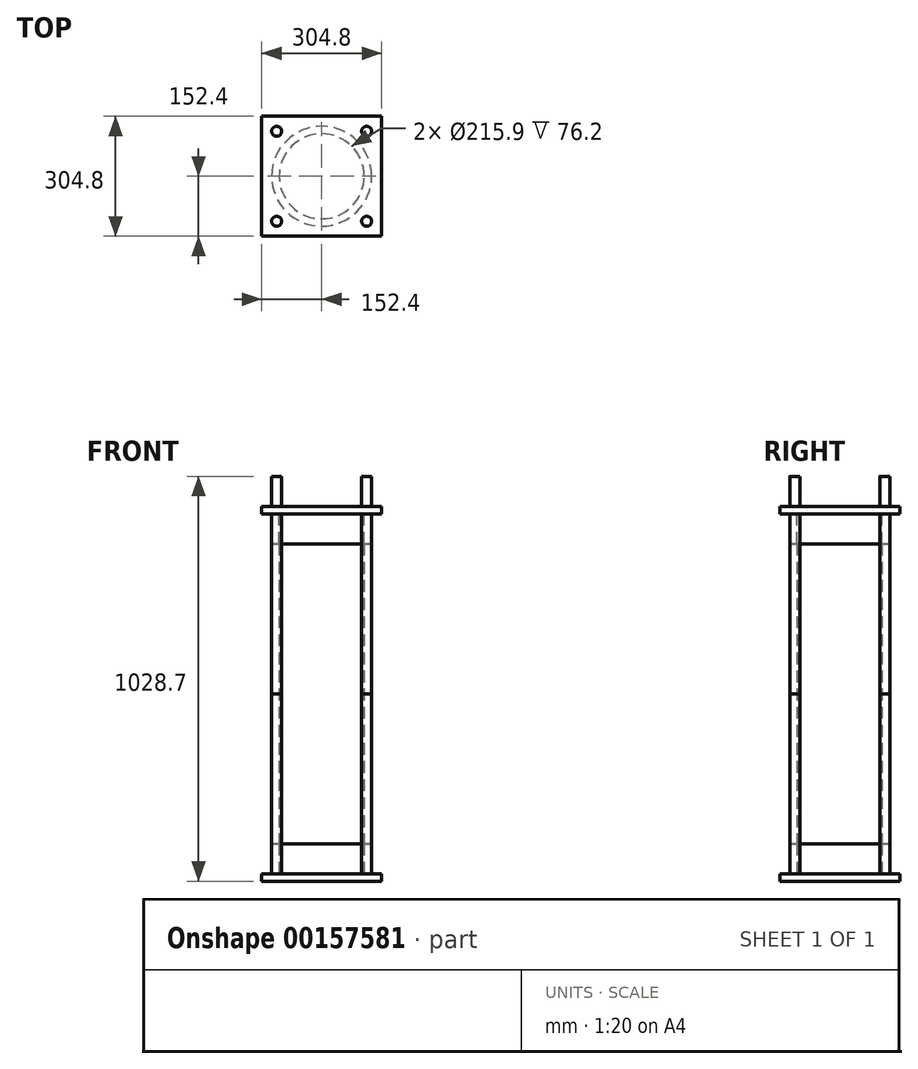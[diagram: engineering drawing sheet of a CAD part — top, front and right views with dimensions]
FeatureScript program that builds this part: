
annotation { "Feature Type Name" : "Feature", "Feature Type Description" : "" }
export const myFeature = defineFeature(function(context is Context, id is Id, definition is map)
    precondition{}
    {
        {
            var Q0;
            Q0=qCreatedBy(makeId("Top.planeOp"),FACE);
            var sketch = newSketch(context, id + "F0", { "sketchPlane" : qUnion([Q0])});
            skLineSegment(sketch, "E0.bottom", {"start": v(0, 0) * mm, "end": v(304.8, 0) * mm});
            skLineSegment(sketch, "E0.top", {"start": v(0, 304.8) * mm, "end": v(304.8, 304.8) * mm});
            skLineSegment(sketch, "E0.left", {"start": v(0, 0) * mm, "end": v(0, 304.8) * mm});
            skLineSegment(sketch, "E0.right", {"start": v(304.8, 0) * mm, "end": v(304.8, 304.8) * mm});
            skSolve(sketch);
        }
        {
            var Q0;
            Q0 = qSketchRegion(id + "F0", true);
            extrude(context, id + "F1", {"entities" : qUnion([Q0]), "depth" : 19.05 * mm});
        }
        {
            var Q0;
            Q0=makeQuery(id+"F1.opExtrude","CAP_FACE",FACE,{"disambiguationData":[OSD([sQuery(id+"F0.wireOp",EDGE,"E0.bottom"),sQuery(id+"F0.wireOp",EDGE,"E0.top"),sQuery(id+"F0.wireOp",EDGE,"E0.left"),sQuery(id+"F0.wireOp",EDGE,"E0.right")])],"isStart":false});
            var sketch = newSketch(context, id + "F2", { "sketchPlane" : qUnion([Q0])});
            skCircle(sketch, "E1", {"center": v(152.4, 152.4) * mm, "radius": 127 * mm});
            skSolve(sketch);
        }
        {
            var Q0;
            Q0 = qSketchRegion(id + "F2", true);
            extrude(context, id + "F3", {"entities" : qUnion([Q0]), "operationType" : NewBodyOperationType.ADD, "depth" : 76.2 * mm});
        }
        {
            var Q0;
            Q0=makeQuery(id+"F3.opExtrude","CAP_FACE",FACE,{"disambiguationData":[OSD([sQuery(id+"F2.wireOp",EDGE,"E1")])],"isStart":false});
            shell(context, id + "F4", {"entities" : qUnion([Q0]), "thickness" : 19.05 * mm});
        }
        {
            var Q0;
            Q0=makeQuery(id+"F1.opExtrude","CAP_FACE",FACE,{"disambiguationData":[OSD([sQuery(id+"F0.wireOp",EDGE,"E0.bottom"),sQuery(id+"F0.wireOp",EDGE,"E0.top"),sQuery(id+"F0.wireOp",EDGE,"E0.left"),sQuery(id+"F0.wireOp",EDGE,"E0.right")])],"isStart":false});
            var sketch = newSketch(context, id + "F5", { "sketchPlane" : qUnion([Q0])});
            skCircle(sketch, "E2", {"center": v(266.7, 266.7) * mm, "radius": 12.7 * mm});
            skCircle(sketch, "E3.0.1.0", {"center": v(266.7, 38.1) * mm, "radius": 12.7 * mm});
            skCircle(sketch, "E3.1.0.0", {"center": v(38.1, 266.7) * mm, "radius": 12.7 * mm});
            skCircle(sketch, "E3.1.1.0", {"center": v(38.1, 38.1) * mm, "radius": 12.7 * mm});
            skLineSegment(sketch, "E3.direction1", {"start": v(266.7, 266.7) * mm, "end": v(38.1, 266.7) * mm, "construction": true});
            skLineSegment(sketch, "E3.direction2", {"start": v(266.7, 266.7) * mm, "end": v(266.7, 38.1) * mm, "construction": true});
            skSolve(sketch);
        }
        {
            var Q0;
            Q0 = qSketchRegion(id + "F5", true);
            extrude(context, id + "F6", {"entities" : qUnion([Q0]), "operationType" : NewBodyOperationType.ADD, "depth" : 457.2 * mm});
        }
        {
            var Q0;
            Q0=makeQuery(id+"F3.opExtrude","CAP_FACE",FACE,{"disambiguationData":[OSD([sQuery(id+"F2.wireOp",EDGE,"E1")])],"isStart":false});
            var sketch = newSketch(context, id + "F7", { "sketchPlane" : qUnion([Q0])});
            skCircle(sketch, "E4", {"center": v(152.4, 152.4) * mm, "radius": 107.95 * mm});
            skSolve(sketch);
        }
        {
            var Q0;
            Q0 = qSketchRegion(id + "F7", true);
            extrude(context, id + "F8", {"entities" : qUnion([Q0]), "depth" : 381 * mm});
        }
        {
            var Q0;
            Q0=makeQuery(id+"F1.opExtrude","SWEPT_BODY",BODY,{"disambiguationData":[OSD([sQuery(id+"F0.wireOp",EDGE,"E0.bottom"),sQuery(id+"F0.wireOp",EDGE,"E0.top"),sQuery(id+"F0.wireOp",EDGE,"E0.left"),sQuery(id+"F0.wireOp",EDGE,"E0.right")])]});
            var Q1;
            Q1=makeQuery(id+"F8.opExtrude","CAP_FACE",FACE,{"disambiguationData":[OSD([sQuery(id+"F7.wireOp",EDGE,"E4")])],"isStart":false});
            mirror(context, id + "F9", {"entities" : qUnion([Q0]), "mirrorPlane" : qUnion([Q1])});
        }
        {
            var Q0;
            Q0=makeQuery(id+"F8.opExtrude","CAP_FACE",FACE,{"disambiguationData":[OSD([sQuery(id+"F7.wireOp",EDGE,"E4")])],"isStart":false});
            var sketch = newSketch(context, id + "F10", { "sketchPlane" : qUnion([Q0])});
            skCircle(sketch, "E5", {"center": v(152.4, 152.4) * mm, "radius": 107.95 * mm});
            skSolve(sketch);
        }
        {
            var Q0;
            Q0 = qSketchRegion(id + "F10", true);
            extrude(context, id + "F11", {"entities" : qUnion([Q0]), "operationType" : NewBodyOperationType.ADD, "depth" : 381 * mm});
        }
        {
            var Q0;
            Q0=makeQuery(id+"F9.opPattern","COPY",FACE,{"derivedFrom":makeQuery(id+"F1.opExtrude","CAP_FACE",FACE,{"disambiguationData":[OSD([sQuery(id+"F0.wireOp",EDGE,"E0.bottom"),sQuery(id+"F0.wireOp",EDGE,"E0.top"),sQuery(id+"F0.wireOp",EDGE,"E0.left"),sQuery(id+"F0.wireOp",EDGE,"E0.right")])],"isStart":true}),"instanceName":"1"});
            var sketch = newSketch(context, id + "F12", { "sketchPlane" : qUnion([Q0])});
            skCircle(sketch, "E6", {"center": v(38.1, 266.7) * mm, "radius": 12.7 * mm});
            skCircle(sketch, "E7.0.1.0", {"center": v(38.1, 38.1) * mm, "radius": 12.7 * mm});
            skCircle(sketch, "E7.1.0.0", {"center": v(266.7, 266.7) * mm, "radius": 12.7 * mm});
            skCircle(sketch, "E7.1.1.0", {"center": v(266.7, 38.1) * mm, "radius": 12.7 * mm});
            skLineSegment(sketch, "E7.direction1", {"start": v(38.1, 266.7) * mm, "end": v(266.7, 266.7) * mm, "construction": true});
            skLineSegment(sketch, "E7.direction2", {"start": v(38.1, 266.7) * mm, "end": v(38.1, 38.1) * mm, "construction": true});
            skSolve(sketch);
        }
        {
            var Q0;
            Q0 = qSketchRegion(id + "F12", true);
            extrude(context, id + "F13", {"entities" : qUnion([Q0]), "operationType" : NewBodyOperationType.ADD, "depth" : 76.2 * mm});
        }
    });
